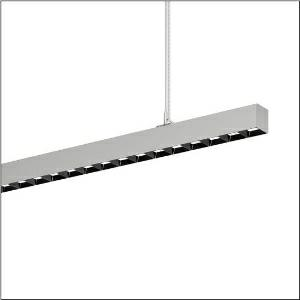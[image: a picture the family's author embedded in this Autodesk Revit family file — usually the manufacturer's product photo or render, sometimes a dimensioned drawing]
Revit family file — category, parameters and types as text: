
# Revit family: silica_r__21_51mx31dc3dsb_b806
name_source: partatom
category: Lighting Fixtures
units: mm (PartAtom-declared; Revit-internal decimal feet)

## family parameters
Cut with Voids When Loaded = No
Host = Face
Light Source = No
Part Type = Normal
Room Calculation Point = No
Round Connector Dimension = Use Diameter
Shared = No

## types (1)
- --- (1 x LED, 18230 lm, 113.3 W, 3000K)
    Apparent Load = 113 VA
    CIE Flux Codes = 87 99 100 59 100
    Color Rendering = 80
    Color Temperature = 3000K
    Default Elevation = 1800 mm
    Description = Silica® 21, office luminaire, primary light control with darklight reflector, of PMMA, black, CAT 2 (L<= 3000cd/m²), light emission: direct/indirect distribution, primary light characteristic: symmetric, installation type: suspended mounting, LED, rated luminous flux: 18.230lm, luminous efficacy: 161lm/W, light colour: 830, colour temperature: 3000K, with terminal, 3+2-pole, max. 2.5mm², mains connection: 220..240V, AC, 50/60Hz, rated input power: 113.3W, luminaire housing, of aluminium, metallic grey (RAL 9006), length: 3.004mm, width: 53mm, height: 53mm, protection rating (complete): IP20, insulation class (complete): insulation class I (protective earthing), certification: CE, permissible operating ambient temperature: 0..+35°C, standard: EN 50419, packaging unit: 1 piece
    Height = 53 mm
    Lamp = 1 x LED
    Lamp Light Flux = 18230 lm
    Lamp Power = 113.3 W
    Lamp count = 1
    Length = 3004 mm
    Luminous efficacy = 161 lm/W
    Manufacturer = Siteco
    ModVariant = No
    Model = 51MX31DC3DSB
    Mounting Place = Ceiling
    Mounting Type = Pendant
    Number of Poles = 1
    OnlyDefault = Yes
    Power Factor = 1
    Product Name = Silica® 21
    Product group = office luminaire | ceiling pendant
    ProductGroupID = 905
    Protection Class = Protection class I
    Protection Degree = IP 20
    RLX_Detail_Level = 1
    RlxData = <blob elided: 65353 chars, md5=aca4e1cb>
    Socket = socket
    Standby Power = 0 W
    System Light Flux = 18230 lm
    System Power = 113 W
    Type Comments = factory setting: luminous flux: 100 % | dim-lin: 254 | 392 mA
    Type Image = l_1251731.jpg
    URL = http://relux.com
    VarID = @adj_029993
    Voltage = 0 V
    Weight = 0.00 kg
    Width = 53 mm

## geometry (parser evidence)
native form markers: Blend x4, Sweep x14
no freeform markers — native parametric forms only
